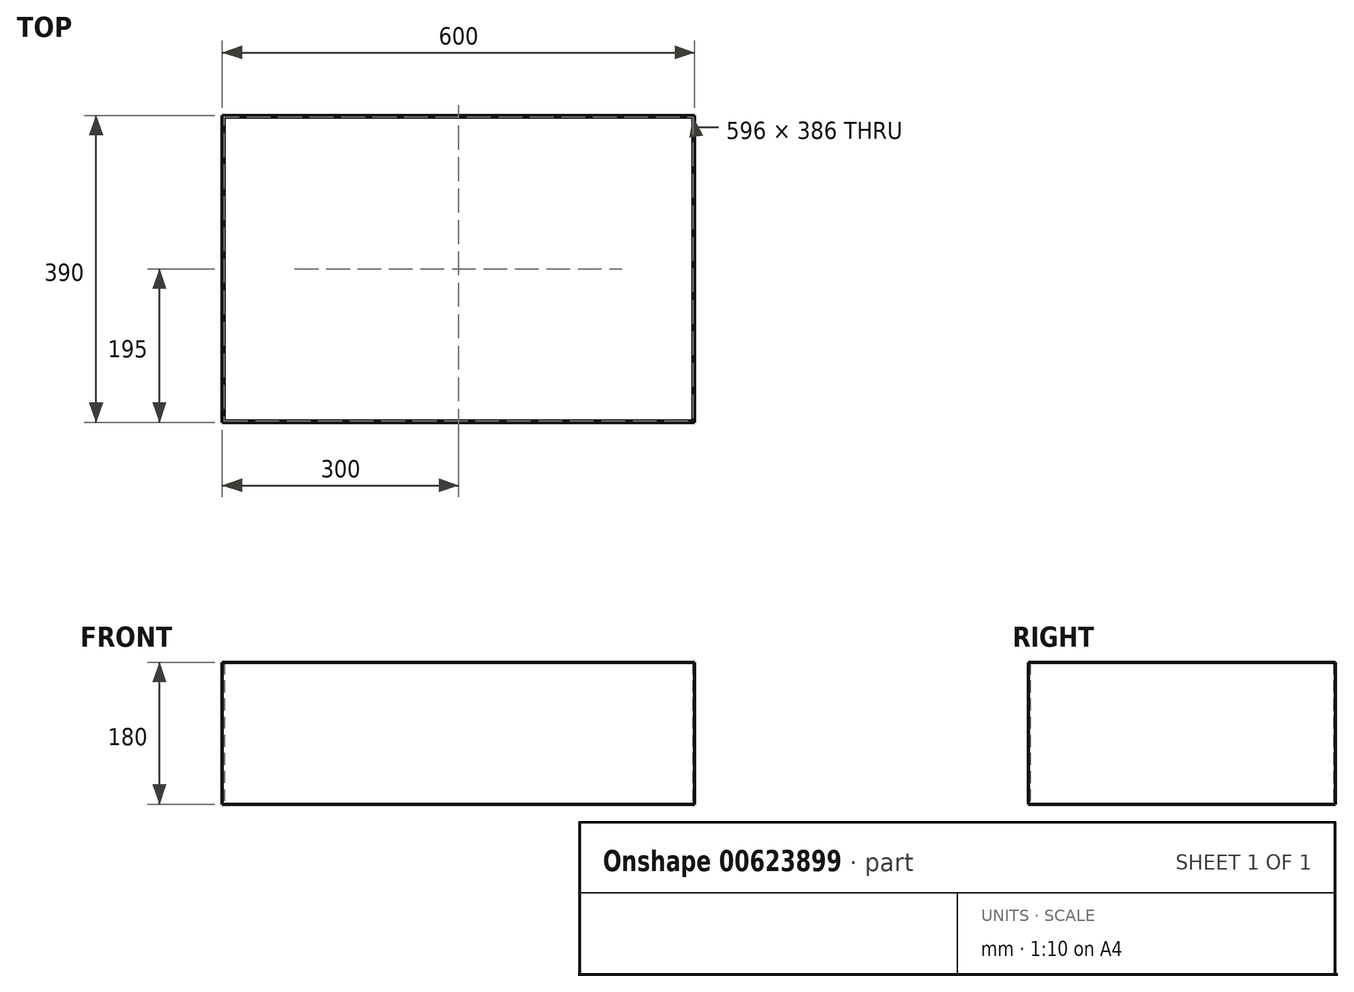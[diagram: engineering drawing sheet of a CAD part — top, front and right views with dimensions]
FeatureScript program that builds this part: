
annotation { "Feature Type Name" : "Feature", "Feature Type Description" : "" }
export const myFeature = defineFeature(function(context is Context, id is Id, definition is map)
    precondition{}
    {
        {
            var Q0;
            Q0=qCreatedBy(makeId("Top.planeOp"),FACE);
            var sketch = newSketch(context, id + "F0", { "sketchPlane" : qUnion([Q0])});
            skLineSegment(sketch, "E0.bottom", {"start": v(0, 0) * mm, "end": v(600, 0) * mm});
            skLineSegment(sketch, "E0.top", {"start": v(0, -390) * mm, "end": v(600, -390) * mm});
            skLineSegment(sketch, "E0.left", {"start": v(0, 0) * mm, "end": v(0, -390) * mm});
            skLineSegment(sketch, "E0.right", {"start": v(600, 0) * mm, "end": v(600, -390) * mm});
            skLineSegment(sketch, "E1.bottom", {"start": v(2, -2) * mm, "end": v(598, -2) * mm});
            skLineSegment(sketch, "E1.top", {"start": v(2, -388) * mm, "end": v(598, -388) * mm});
            skLineSegment(sketch, "E1.left", {"start": v(2, -2) * mm, "end": v(2, -388) * mm});
            skLineSegment(sketch, "E1.right", {"start": v(598, -2) * mm, "end": v(598, -388) * mm});
            skSolve(sketch);
        }
        {
            var Q0;
            Q0 = qSketchRegion(id + "F0", true);
            extrude(context, id + "F1", {"entities" : qUnion([Q0]), "depth" : 180 * mm, "offsetDistance" : 25 * mm});
        }
    });
